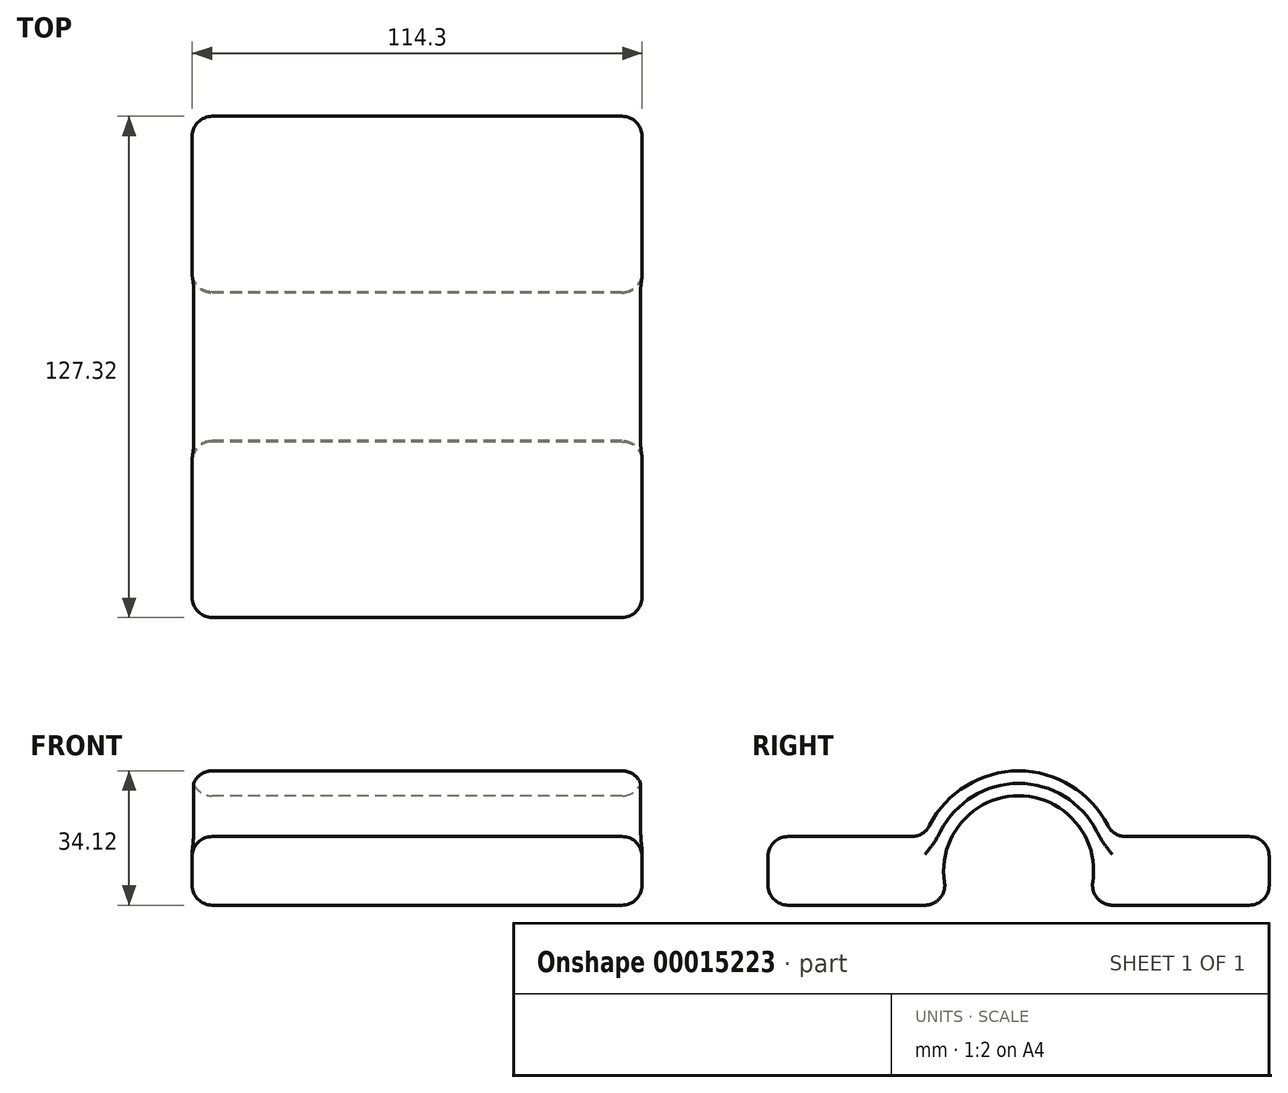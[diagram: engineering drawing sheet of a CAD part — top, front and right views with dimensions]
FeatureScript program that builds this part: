
annotation { "Feature Type Name" : "Feature", "Feature Type Description" : "" }
export const myFeature = defineFeature(function(context is Context, id is Id, definition is map)
    precondition{}
    {
        {
            var Q0;
            Q0=qCreatedBy(makeId("Right.planeOp"),FACE);
            var sketch = newSketch(context, id + "F0", { "sketchPlane" : qUnion([Q0])});
            skLineSegment(sketch, "E0", {"start": v(80.32, 0) * mm, "end": v(-81.48, 0) * mm, "construction": true});
            skArc(sketch, "E1", {"start": v(16.94, -8.72) * mm, "mid": v(0, 19.05) * mm, "end": v(-16.94, -8.72) * mm});
            skLineSegment(sketch, "E2", {"start": v(-16.94, 8.72) * mm, "end": v(-63.66, 8.72) * mm});
            skLineSegment(sketch, "E3", {"start": v(-63.66, 8.72) * mm, "end": v(-63.66, -8.72) * mm});
            skLineSegment(sketch, "E4", {"start": v(-63.66, -8.72) * mm, "end": v(-16.94, -8.72) * mm});
            skLineSegment(sketch, "E5", {"start": v(16.94, 8.72) * mm, "end": v(63.66, 8.72) * mm});
            skLineSegment(sketch, "E6", {"start": v(63.66, 8.72) * mm, "end": v(63.66, -8.72) * mm});
            skLineSegment(sketch, "E7", {"start": v(63.66, -8.72) * mm, "end": v(16.94, -8.72) * mm});
            skLineSegment(sketch, "E8", {"start": v(-16.94, -8.72) * mm, "end": v(16.94, -8.72) * mm, "construction": true});
            skArc(sketch, "E9.0", {"start": v(23.86, -8.72) * mm, "mid": v(0, 25.4) * mm, "end": v(-23.86, -8.72) * mm});
            skSolve(sketch);
        }
        {
            var Q0;
            Q0 = qSketchRegion(id + "F0", true);
            extrude(context, id + "F1", {"entities" : qUnion([Q0]), "endBound" : BoundingType.SYMMETRIC, "depth" : 114.3 * mm});
        }
        {
            var Q0;
            Q0=makeQuery(id+"F1.opExtrude","CAP_FACE",FACE,{"disambiguationData":[OSD([sQuery(id+"F0.wireOp",EDGE,"E1"),sQuery(id+"F0.wireOp",EDGE,"E2"),sQuery(id+"F0.wireOp",EDGE,"E3"),sQuery(id+"F0.wireOp",EDGE,"E4"),sQuery(id+"F0.wireOp",EDGE,"E5"),sQuery(id+"F0.wireOp",EDGE,"E6"),sQuery(id+"F0.wireOp",EDGE,"E7"),sQuery(id+"F0.wireOp",EDGE,"E9.0")])],"isStart":true});
            var Q1;
            Q1=makeQuery(id+"F1.opExtrude","SWEPT_FACE",FACE,{"disambiguationData":[OSD([sQuery(id+"F0.wireOp",EDGE,"E7")])]});
            var Q2;
            Q2=makeQuery(id+"F1.opExtrude","SWEPT_FACE",FACE,{"disambiguationData":[OSD([sQuery(id+"F0.wireOp",EDGE,"E4")])]});
            var Q3;
            Q3=makeQuery(id+"F1.opExtrude","SWEPT_FACE",FACE,{"disambiguationData":[OSD([sQuery(id+"F0.wireOp",EDGE,"E2")])]});
            var Q4;
            Q4=makeQuery(id+"F1.opExtrude","SWEPT_FACE",FACE,{"disambiguationData":[OSD([sQuery(id+"F0.wireOp",EDGE,"E5")])]});
            var Q5;
            Q5=makeQuery(id+"F1.opExtrude","SWEPT_FACE",FACE,{"disambiguationData":[OSD([sQuery(id+"F0.wireOp",EDGE,"E9.0")])]});
            var Q6;
            Q6=makeQuery(id+"F1.opExtrude","SWEPT_FACE",FACE,{"disambiguationData":[OSD([sQuery(id+"F0.wireOp",EDGE,"E1")])]});
            fillet(context, id + "F2", {"entities" : qUnion([Q0, Q1, Q2, Q3, Q4, Q5, Q6]), "radius" : 5.08 * mm, "tangentPropagation" : true, "allowEdgeOverflow" : false});
        }
        {
            var Q0;
            {var subQ0=sQuery(id+"F0.wireOp",EDGE,"E5");Q0=makeQuery(id+"F2.opFillet","BLEND_EDGE",EDGE,{"blendedFrom":[makeQuery(id+"F1.opExtrude","SWEPT_EDGE",EDGE,{"disambiguationData":[OSD([subQ0,sQuery(id+"F0.wireOp",EDGE,"E6")])]}),makeQuery(id+"F1.opExtrude","CAP_EDGE",EDGE,{"disambiguationData":[OSD([subQ0])],"isStart":false})],"blendedInto":[]});}
            var Q1;
            {var subQ0=sQuery(id+"F0.wireOp",EDGE,"E2");Q1=makeQuery(id+"F2.opFillet","BLEND_EDGE",EDGE,{"blendedFrom":[makeQuery(id+"F1.opExtrude","SWEPT_EDGE",EDGE,{"disambiguationData":[OSD([subQ0,sQuery(id+"F0.wireOp",EDGE,"E3")])]}),makeQuery(id+"F1.opExtrude","CAP_EDGE",EDGE,{"disambiguationData":[OSD([subQ0])],"isStart":false})],"blendedInto":[]});}
            fillet(context, id + "F3", {"entities" : qUnion([Q0, Q1]), "radius" : 5.08 * mm, "tangentPropagation" : true, "allowEdgeOverflow" : false});
        }
    });
